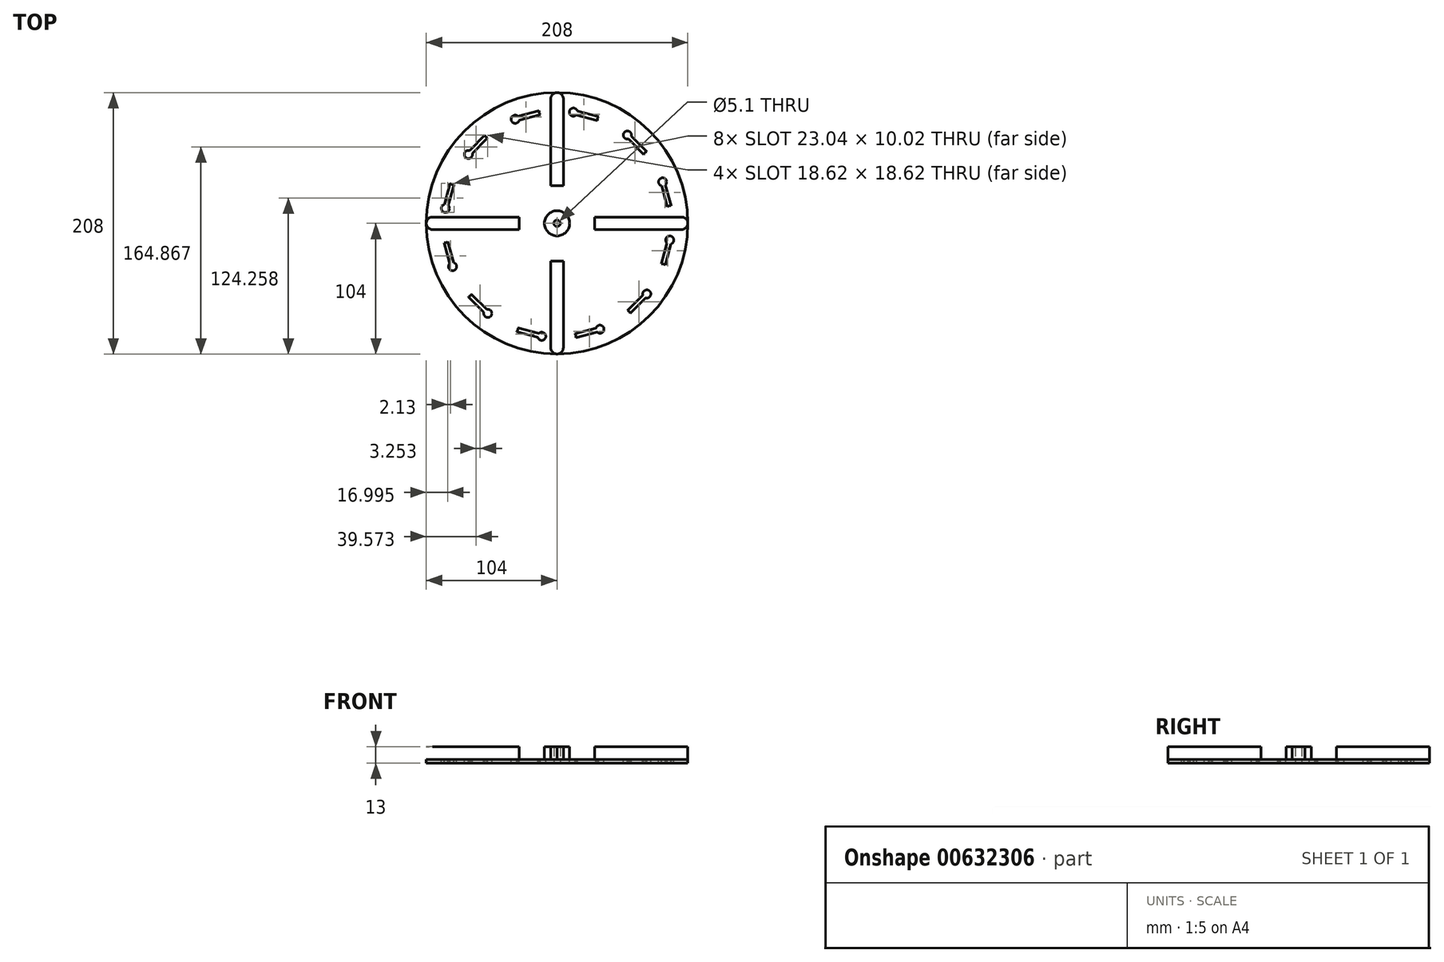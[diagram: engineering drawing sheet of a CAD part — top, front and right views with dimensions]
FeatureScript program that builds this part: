
annotation { "Feature Type Name" : "Feature", "Feature Type Description" : "" }
export const myFeature = defineFeature(function(context is Context, id is Id, definition is map)
    precondition{}
    {
        {
            var Q0;
            Q0=qCreatedBy(makeId("Top.planeOp"),FACE);
            var sketch = newSketch(context, id + "F0", { "sketchPlane" : qUnion([Q0])});
            skCircle(sketch, "E0", {"center": v(0, 0) * mm, "radius": 104 * mm});
            skSolve(sketch);
        }
        {
            var Q0;
            Q0 = qSketchRegion(id + "F0", true);
            extrude(context, id + "F1", {"entities" : qUnion([Q0]), "depth" : 3 * mm, "offsetDistance" : 25 * mm});
        }
        {
            var Q0;
            Q0=makeQuery(id+"F1.opExtrude","CAP_FACE",FACE,{"disambiguationData":[OSD([sQuery(id+"F0.wireOp",EDGE,"E0")])],"isStart":false});
            var sketch = newSketch(context, id + "F2", { "sketchPlane" : qUnion([Q0])});
            skLineSegment(sketch, "E1.bottom", {"start": v(-30, -5) * mm, "end": v(-99, -5) * mm});
            skLineSegment(sketch, "E1.top", {"start": v(-30, 5) * mm, "end": v(-99, 5) * mm});
            skLineSegment(sketch, "E1.left", {"start": v(-30, -5) * mm, "end": v(-30, 5) * mm});
            skLineSegment(sketch, "E1.right", {"start": v(-99, -5) * mm, "end": v(-99, 5) * mm});
            skPoint(sketch, "E1.middle", {"position": v(-64.5, 0) * mm});
            skArc(sketch, "E2", {"start": v(-99, -5) * mm, "mid": v(-104, 0) * mm, "end": v(-99, 5) * mm});
            skLineSegment(sketch, "E3.1.0", {"start": v(-5, -30) * mm, "end": v(-5, -99) * mm});
            skLineSegment(sketch, "E3.1.1", {"start": v(5, -30) * mm, "end": v(5, -99) * mm});
            skArc(sketch, "E3.1.2", {"start": v(5, -99) * mm, "mid": v(0, -104) * mm, "end": v(-5, -99) * mm});
            skLineSegment(sketch, "E3.1.3", {"start": v(5, -30) * mm, "end": v(-5, -30) * mm});
            skLineSegment(sketch, "E3.2.0", {"start": v(30, -5) * mm, "end": v(99, -5) * mm});
            skLineSegment(sketch, "E3.2.1", {"start": v(30, 5) * mm, "end": v(99, 5) * mm});
            skArc(sketch, "E3.2.2", {"start": v(99, 5) * mm, "mid": v(104, 0) * mm, "end": v(99, -5) * mm});
            skLineSegment(sketch, "E3.2.3", {"start": v(30, 5) * mm, "end": v(30, -5) * mm});
            skLineSegment(sketch, "E3.3.0", {"start": v(5, 30) * mm, "end": v(5, 99) * mm});
            skLineSegment(sketch, "E3.3.1", {"start": v(-5, 30) * mm, "end": v(-5, 99) * mm});
            skArc(sketch, "E3.3.2", {"start": v(-5, 99) * mm, "mid": v(0, 104) * mm, "end": v(5, 99) * mm});
            skLineSegment(sketch, "E3.3.3", {"start": v(-5, 30) * mm, "end": v(5, 30) * mm});
            skPoint(sketch, "E4.center", {"position": v(0, 0) * mm});
            skCircle(sketch, "E5", {"center": v(-34.4, -83.96) * mm, "radius": 3.25 * mm});
            skLineSegment(sketch, "E6", {"start": v(-22.88, -85.39) * mm, "end": v(-31.26, -83.14) * mm});
            skLineSegment(sketch, "E7", {"start": v(-34.4, -83.96) * mm, "end": v(-23.3, -86.93) * mm, "construction": true});
            skLineSegment(sketch, "E8.MirrorCS", {"start": v(-23.7, -88.48) * mm, "end": v(-32.08, -86.23) * mm});
            skLineSegment(sketch, "E9.MirrorCS", {"start": v(-45.97, -171.57) * mm, "end": v(-17.63, -65.8) * mm, "construction": true});
            skLineSegment(sketch, "E10.MirrorCS", {"start": v(-22.88, -85.39) * mm, "end": v(-14.5, -87.63) * mm});
            skLineSegment(sketch, "E11.MirrorCS", {"start": v(-23.7, -88.48) * mm, "end": v(-15.33, -90.72) * mm});
            skCircle(sketch, "E12.MirrorC", {"center": v(-12.19, -89.9) * mm, "radius": 3.25 * mm});
            skLineSegment(sketch, "E13.1.0", {"start": v(22.57, -85.7) * mm, "end": v(14.2, -87.94) * mm});
            skLineSegment(sketch, "E13.1.1", {"start": v(23.4, -88.79) * mm, "end": v(15.03, -91.03) * mm});
            skCircle(sketch, "E13.1.2", {"center": v(11.88, -90.22) * mm, "radius": 3.25 * mm});
            skLineSegment(sketch, "E13.1.3", {"start": v(23.4, -88.79) * mm, "end": v(31.78, -86.54) * mm});
            skLineSegment(sketch, "E13.1.4", {"start": v(22.57, -85.7) * mm, "end": v(30.95, -83.45) * mm});
            skCircle(sketch, "E13.1.5", {"center": v(34.1, -84.26) * mm, "radius": 3.25 * mm});
            skLineSegment(sketch, "E13.2.0", {"start": v(62.09, -63.23) * mm, "end": v(55.96, -69.37) * mm});
            skLineSegment(sketch, "E13.2.1", {"start": v(64.35, -65.5) * mm, "end": v(58.22, -71.63) * mm});
            skCircle(sketch, "E13.2.2", {"center": v(55.09, -72.5) * mm, "radius": 3.25 * mm});
            skLineSegment(sketch, "E13.2.3", {"start": v(64.35, -65.5) * mm, "end": v(70.48, -59.37) * mm});
            skLineSegment(sketch, "E13.2.4", {"start": v(62.09, -63.23) * mm, "end": v(68.22, -57.1) * mm});
            skCircle(sketch, "E13.2.5", {"center": v(71.35, -56.23) * mm, "radius": 3.25 * mm});
            skLineSegment(sketch, "E13.3.0", {"start": v(85.08, -24.03) * mm, "end": v(82.84, -32.4) * mm});
            skLineSegment(sketch, "E13.3.1", {"start": v(88.17, -24.85) * mm, "end": v(85.93, -33.23) * mm});
            skCircle(sketch, "E13.3.2", {"center": v(83.65, -35.55) * mm, "radius": 3.25 * mm});
            skLineSegment(sketch, "E13.3.3", {"start": v(88.17, -24.85) * mm, "end": v(90.42, -16.48) * mm});
            skLineSegment(sketch, "E13.3.4", {"start": v(85.08, -24.03) * mm, "end": v(87.32, -15.65) * mm});
            skCircle(sketch, "E13.3.5", {"center": v(89.6, -13.33) * mm, "radius": 3.25 * mm});
            skLineSegment(sketch, "E13.4.0", {"start": v(85.39, 21.43) * mm, "end": v(87.63, 13.05) * mm});
            skLineSegment(sketch, "E13.4.1", {"start": v(88.48, 22.25) * mm, "end": v(90.72, 13.88) * mm});
            skCircle(sketch, "E13.4.2", {"center": v(89.9, 10.73) * mm, "radius": 3.25 * mm});
            skLineSegment(sketch, "E13.4.3", {"start": v(88.48, 22.25) * mm, "end": v(86.23, 30.63) * mm});
            skLineSegment(sketch, "E13.4.4", {"start": v(85.39, 21.43) * mm, "end": v(83.14, 29.8) * mm});
            skCircle(sketch, "E13.4.5", {"center": v(83.96, 32.95) * mm, "radius": 3.25 * mm});
            skLineSegment(sketch, "E13.5.0", {"start": v(62.93, 60.94) * mm, "end": v(69.06, 54.81) * mm});
            skLineSegment(sketch, "E13.5.1", {"start": v(65.2, 63.2) * mm, "end": v(71.32, 57.07) * mm});
            skCircle(sketch, "E13.5.2", {"center": v(72.2, 53.94) * mm, "radius": 3.25 * mm});
            skLineSegment(sketch, "E13.5.3", {"start": v(65.2, 63.2) * mm, "end": v(59.06, 69.34) * mm});
            skLineSegment(sketch, "E13.5.4", {"start": v(62.93, 60.94) * mm, "end": v(56.8, 67.07) * mm});
            skCircle(sketch, "E13.5.5", {"center": v(55.93, 70.2) * mm, "radius": 3.25 * mm});
            skLineSegment(sketch, "E13.6.0", {"start": v(23.72, 83.93) * mm, "end": v(32.1, 81.69) * mm});
            skLineSegment(sketch, "E13.6.1", {"start": v(24.55, 87.03) * mm, "end": v(32.92, 84.78) * mm});
            skCircle(sketch, "E13.6.2", {"center": v(35.24, 82.5) * mm, "radius": 3.25 * mm});
            skLineSegment(sketch, "E13.6.3", {"start": v(24.55, 87.03) * mm, "end": v(16.17, 89.27) * mm});
            skLineSegment(sketch, "E13.6.4", {"start": v(23.72, 83.93) * mm, "end": v(15.34, 86.18) * mm});
            skCircle(sketch, "E13.6.5", {"center": v(13.02, 88.46) * mm, "radius": 3.25 * mm});
            skLineSegment(sketch, "E13.7.0", {"start": v(-21.73, 84.24) * mm, "end": v(-13.36, 86.49) * mm});
            skLineSegment(sketch, "E13.7.1", {"start": v(-22.56, 87.33) * mm, "end": v(-14.19, 89.58) * mm});
            skCircle(sketch, "E13.7.2", {"center": v(-11.04, 88.76) * mm, "radius": 3.25 * mm});
            skLineSegment(sketch, "E13.7.3", {"start": v(-22.56, 87.33) * mm, "end": v(-30.94, 85.09) * mm});
            skLineSegment(sketch, "E13.7.4", {"start": v(-21.73, 84.24) * mm, "end": v(-30.1, 82) * mm});
            skCircle(sketch, "E13.7.5", {"center": v(-33.26, 82.81) * mm, "radius": 3.25 * mm});
            skLineSegment(sketch, "E13.8.0", {"start": v(-61.25, 61.78) * mm, "end": v(-55.12, 67.91) * mm});
            skLineSegment(sketch, "E13.8.1", {"start": v(-63.51, 64.04) * mm, "end": v(-57.38, 70.18) * mm});
            skCircle(sketch, "E13.8.2", {"center": v(-54.25, 71.04) * mm, "radius": 3.25 * mm});
            skLineSegment(sketch, "E13.8.3", {"start": v(-63.51, 64.04) * mm, "end": v(-69.64, 57.91) * mm});
            skLineSegment(sketch, "E13.8.4", {"start": v(-61.25, 61.78) * mm, "end": v(-67.38, 55.65) * mm});
            skCircle(sketch, "E13.8.5", {"center": v(-70.51, 54.78) * mm, "radius": 3.25 * mm});
            skLineSegment(sketch, "E13.9.0", {"start": v(-84.24, 22.57) * mm, "end": v(-82, 30.95) * mm});
            skLineSegment(sketch, "E13.9.1", {"start": v(-87.33, 23.4) * mm, "end": v(-85.09, 31.78) * mm});
            skCircle(sketch, "E13.9.2", {"center": v(-82.81, 34.1) * mm, "radius": 3.25 * mm});
            skLineSegment(sketch, "E13.9.3", {"start": v(-87.33, 23.4) * mm, "end": v(-89.58, 15.02) * mm});
            skLineSegment(sketch, "E13.9.4", {"start": v(-84.24, 22.57) * mm, "end": v(-86.49, 14.2) * mm});
            skCircle(sketch, "E13.9.5", {"center": v(-88.76, 11.88) * mm, "radius": 3.25 * mm});
            skLineSegment(sketch, "E13.10.0", {"start": v(-84.55, -22.88) * mm, "end": v(-86.8, -14.5) * mm});
            skLineSegment(sketch, "E13.10.1", {"start": v(-87.64, -23.7) * mm, "end": v(-89.88, -15.33) * mm});
            skCircle(sketch, "E13.10.2", {"center": v(-89.07, -12.19) * mm, "radius": 3.25 * mm});
            skLineSegment(sketch, "E13.10.3", {"start": v(-87.64, -23.7) * mm, "end": v(-85.4, -32.08) * mm});
            skLineSegment(sketch, "E13.10.4", {"start": v(-84.55, -22.88) * mm, "end": v(-82.3, -31.26) * mm});
            skCircle(sketch, "E13.10.5", {"center": v(-83.12, -34.4) * mm, "radius": 3.25 * mm});
            skLineSegment(sketch, "E13.11.0", {"start": v(-62.09, -62.4) * mm, "end": v(-68.22, -56.26) * mm});
            skLineSegment(sketch, "E13.11.1", {"start": v(-64.35, -64.66) * mm, "end": v(-70.48, -58.53) * mm});
            skCircle(sketch, "E13.11.2", {"center": v(-71.35, -55.4) * mm, "radius": 3.25 * mm});
            skLineSegment(sketch, "E13.11.3", {"start": v(-64.35, -64.66) * mm, "end": v(-58.22, -70.8) * mm});
            skLineSegment(sketch, "E13.11.4", {"start": v(-62.09, -62.4) * mm, "end": v(-55.96, -68.53) * mm});
            skCircle(sketch, "E13.11.5", {"center": v(-55.09, -71.66) * mm, "radius": 3.25 * mm});
            skLineSegment(sketch, "E14", {"start": v(0, 0) * mm, "end": v(-23.3, -86.93) * mm, "construction": true});
            skCircle(sketch, "E15", {"center": v(0, 0) * mm, "radius": 10 * mm});
            skCircle(sketch, "E16", {"center": v(0, 0) * mm, "radius": 2.55 * mm});
            skSolve(sketch);
        }
        {
            var Q0;
            Q0=makeQuery(id+"F2.imprint","IMPRINT",FACE,{"disambiguationData":[TD([[makeQuery(id+"F2.imprint","IMPRINT",EDGE,{"derivedFrom":sQuery(id+"F2.wireOp",EDGE,"E1.bottom")}),-1.0]])]});
            var Q1;
            {var subQ0=sQuery(id+"F2.wireOp",EDGE,"E1.right");Q1=makeQuery(id+"F2.imprint","IMPRINT",FACE,{"disambiguationData":[TD([[makeQuery(id+"F2.imprint","IMPRINT",EDGE,{"derivedFrom":subQ0}),1.0]])]});}
            var Q2;
            Q2=makeQuery(id+"F2.imprint","IMPRINT",FACE,{"disambiguationData":[TD([[makeQuery(id+"F2.imprint","IMPRINT",EDGE,{"derivedFrom":sQuery(id+"F2.wireOp",EDGE,"1YY4uECu-RtR1-OI2Z-D8cp-1v98Y9N5imrY")}),1.0]])]});
            var Q3;
            {var subQ1=sQuery(id+"F2.wireOp",EDGE,"E3.3.0");Q3=makeQuery(id+"F2.imprint","IMPRINT",FACE,{"disambiguationData":[TD([[makeQuery(id+"F2.imprint","IMPRINT",EDGE,{"derivedFrom":subQ1}),1.0]])]});}
            var Q4;
            {var subQ1=sQuery(id+"F2.wireOp",EDGE,"E3.1.0");Q4=makeQuery(id+"F2.imprint","IMPRINT",FACE,{"disambiguationData":[TD([[makeQuery(id+"F2.imprint","IMPRINT",EDGE,{"derivedFrom":subQ1}),1.0]])]});}
            var Q5;
            {var subQ1=sQuery(id+"F2.wireOp",EDGE,"E3.2.0");Q5=makeQuery(id+"F2.imprint","IMPRINT",FACE,{"disambiguationData":[TD([[makeQuery(id+"F2.imprint","IMPRINT",EDGE,{"derivedFrom":subQ1}),1.0]])]});}
            var Q6;
            Q6=makeQuery(id+"F2.imprint","IMPRINT",FACE,{"disambiguationData":[TD([[makeQuery(id+"F2.imprint","IMPRINT",EDGE,{"derivedFrom":sQuery(id+"F2.wireOp",EDGE,"E15")}),1.0]])]});
            extrude(context, id + "F3", {"entities" : qUnion([Q0, Q1, Q2, Q3, Q4, Q5, Q6]), "operationType" : NewBodyOperationType.ADD, "depth" : 10 * mm, "offsetDistance" : 25 * mm});
        }
        {
            var Q0;
            {var subQ0=sQuery(id+"F2.wireOp",EDGE,"E13.9.5");var subQ1=makeQuery(id+"F2.imprint","INTERSECT",VERTEX,{"derivedFrom":[sQuery(id+"F2.wireOp",EDGE,"E13.9.3"),subQ0]});Q0=makeQuery(id+"F2.imprint","IMPRINT",FACE,{"disambiguationData":[TD([[makeQuery(id+"F2.imprint","IMPRINT",EDGE,{"disambiguationData":[TD([[subQ1,-1.0]])],"derivedFrom":subQ0}),1.0]])]});}
            var Q1;
            {var subQ2=sQuery(id+"F2.wireOp",EDGE,"E13.9.0");Q1=makeQuery(id+"F2.imprint","IMPRINT",FACE,{"disambiguationData":[TD([[makeQuery(id+"F2.imprint","IMPRINT",EDGE,{"derivedFrom":subQ2}),1.0]])]});}
            var Q2;
            {var subQ0=sQuery(id+"F2.wireOp",EDGE,"E13.9.2");var subQ1=makeQuery(id+"F2.imprint","INTERSECT",VERTEX,{"derivedFrom":[sQuery(id+"F2.wireOp",EDGE,"E13.9.0"),subQ0]});Q2=makeQuery(id+"F2.imprint","IMPRINT",FACE,{"disambiguationData":[TD([[makeQuery(id+"F2.imprint","IMPRINT",EDGE,{"disambiguationData":[TD([[subQ1,1.0]])],"derivedFrom":subQ0}),-1.0]])]});}
            var Q3;
            {var subQ0=sQuery(id+"F2.wireOp",EDGE,"E13.8.5");var subQ1=makeQuery(id+"F2.imprint","INTERSECT",VERTEX,{"derivedFrom":[sQuery(id+"F2.wireOp",EDGE,"E13.8.3"),subQ0]});Q3=makeQuery(id+"F2.imprint","IMPRINT",FACE,{"disambiguationData":[TD([[makeQuery(id+"F2.imprint","IMPRINT",EDGE,{"disambiguationData":[TD([[subQ1,-1.0]])],"derivedFrom":subQ0}),1.0]])]});}
            var Q4;
            {var subQ2=sQuery(id+"F2.wireOp",EDGE,"E13.8.0");Q4=makeQuery(id+"F2.imprint","IMPRINT",FACE,{"disambiguationData":[TD([[makeQuery(id+"F2.imprint","IMPRINT",EDGE,{"derivedFrom":subQ2}),1.0]])]});}
            var Q5;
            {var subQ0=sQuery(id+"F2.wireOp",EDGE,"E13.8.2");var subQ1=makeQuery(id+"F2.imprint","INTERSECT",VERTEX,{"derivedFrom":[sQuery(id+"F2.wireOp",EDGE,"E13.8.0"),subQ0]});Q5=makeQuery(id+"F2.imprint","IMPRINT",FACE,{"disambiguationData":[TD([[makeQuery(id+"F2.imprint","IMPRINT",EDGE,{"disambiguationData":[TD([[subQ1,1.0]])],"derivedFrom":subQ0}),-1.0]])]});}
            var Q6;
            {var subQ0=sQuery(id+"F2.wireOp",EDGE,"E13.7.5");var subQ1=makeQuery(id+"F2.imprint","INTERSECT",VERTEX,{"derivedFrom":[sQuery(id+"F2.wireOp",EDGE,"E13.7.3"),subQ0]});Q6=makeQuery(id+"F2.imprint","IMPRINT",FACE,{"disambiguationData":[TD([[makeQuery(id+"F2.imprint","IMPRINT",EDGE,{"disambiguationData":[TD([[subQ1,-1.0]])],"derivedFrom":subQ0}),1.0]])]});}
            var Q7;
            {var subQ2=sQuery(id+"F2.wireOp",EDGE,"E13.7.0");Q7=makeQuery(id+"F2.imprint","IMPRINT",FACE,{"disambiguationData":[TD([[makeQuery(id+"F2.imprint","IMPRINT",EDGE,{"derivedFrom":subQ2}),1.0]])]});}
            var Q8;
            {var subQ0=sQuery(id+"F2.wireOp",EDGE,"E13.7.2");var subQ1=makeQuery(id+"F2.imprint","INTERSECT",VERTEX,{"derivedFrom":[sQuery(id+"F2.wireOp",EDGE,"E13.7.0"),subQ0]});Q8=makeQuery(id+"F2.imprint","IMPRINT",FACE,{"disambiguationData":[TD([[makeQuery(id+"F2.imprint","IMPRINT",EDGE,{"disambiguationData":[TD([[subQ1,1.0]])],"derivedFrom":subQ0}),-1.0]])]});}
            var Q9;
            {var subQ0=sQuery(id+"F2.wireOp",EDGE,"E13.6.5");var subQ1=makeQuery(id+"F2.imprint","INTERSECT",VERTEX,{"derivedFrom":[sQuery(id+"F2.wireOp",EDGE,"E13.6.3"),subQ0]});Q9=makeQuery(id+"F2.imprint","IMPRINT",FACE,{"disambiguationData":[TD([[makeQuery(id+"F2.imprint","IMPRINT",EDGE,{"disambiguationData":[TD([[subQ1,-1.0]])],"derivedFrom":subQ0}),1.0]])]});}
            var Q10;
            {var subQ2=sQuery(id+"F2.wireOp",EDGE,"E13.6.0");Q10=makeQuery(id+"F2.imprint","IMPRINT",FACE,{"disambiguationData":[TD([[makeQuery(id+"F2.imprint","IMPRINT",EDGE,{"derivedFrom":subQ2}),1.0]])]});}
            var Q11;
            {var subQ0=sQuery(id+"F2.wireOp",EDGE,"E13.6.2");var subQ1=makeQuery(id+"F2.imprint","INTERSECT",VERTEX,{"derivedFrom":[sQuery(id+"F2.wireOp",EDGE,"E13.6.0"),subQ0]});Q11=makeQuery(id+"F2.imprint","IMPRINT",FACE,{"disambiguationData":[TD([[makeQuery(id+"F2.imprint","IMPRINT",EDGE,{"disambiguationData":[TD([[subQ1,1.0]])],"derivedFrom":subQ0}),-1.0]])]});}
            var Q12;
            {var subQ0=sQuery(id+"F2.wireOp",EDGE,"E13.5.5");var subQ1=makeQuery(id+"F2.imprint","INTERSECT",VERTEX,{"derivedFrom":[sQuery(id+"F2.wireOp",EDGE,"E13.5.3"),subQ0]});Q12=makeQuery(id+"F2.imprint","IMPRINT",FACE,{"disambiguationData":[TD([[makeQuery(id+"F2.imprint","IMPRINT",EDGE,{"disambiguationData":[TD([[subQ1,-1.0]])],"derivedFrom":subQ0}),1.0]])]});}
            var Q13;
            {var subQ2=sQuery(id+"F2.wireOp",EDGE,"E13.5.0");Q13=makeQuery(id+"F2.imprint","IMPRINT",FACE,{"disambiguationData":[TD([[makeQuery(id+"F2.imprint","IMPRINT",EDGE,{"derivedFrom":subQ2}),1.0]])]});}
            var Q14;
            {var subQ0=sQuery(id+"F2.wireOp",EDGE,"E13.5.2");var subQ1=makeQuery(id+"F2.imprint","INTERSECT",VERTEX,{"derivedFrom":[sQuery(id+"F2.wireOp",EDGE,"E13.5.0"),subQ0]});Q14=makeQuery(id+"F2.imprint","IMPRINT",FACE,{"disambiguationData":[TD([[makeQuery(id+"F2.imprint","IMPRINT",EDGE,{"disambiguationData":[TD([[subQ1,1.0]])],"derivedFrom":subQ0}),-1.0]])]});}
            var Q15;
            {var subQ0=sQuery(id+"F2.wireOp",EDGE,"E13.4.5");var subQ1=makeQuery(id+"F2.imprint","INTERSECT",VERTEX,{"derivedFrom":[sQuery(id+"F2.wireOp",EDGE,"E13.4.3"),subQ0]});Q15=makeQuery(id+"F2.imprint","IMPRINT",FACE,{"disambiguationData":[TD([[makeQuery(id+"F2.imprint","IMPRINT",EDGE,{"disambiguationData":[TD([[subQ1,-1.0]])],"derivedFrom":subQ0}),1.0]])]});}
            var Q16;
            {var subQ2=sQuery(id+"F2.wireOp",EDGE,"E13.4.0");Q16=makeQuery(id+"F2.imprint","IMPRINT",FACE,{"disambiguationData":[TD([[makeQuery(id+"F2.imprint","IMPRINT",EDGE,{"derivedFrom":subQ2}),1.0]])]});}
            var Q17;
            {var subQ0=sQuery(id+"F2.wireOp",EDGE,"E13.4.2");var subQ1=makeQuery(id+"F2.imprint","INTERSECT",VERTEX,{"derivedFrom":[sQuery(id+"F2.wireOp",EDGE,"E13.4.0"),subQ0]});Q17=makeQuery(id+"F2.imprint","IMPRINT",FACE,{"disambiguationData":[TD([[makeQuery(id+"F2.imprint","IMPRINT",EDGE,{"disambiguationData":[TD([[subQ1,1.0]])],"derivedFrom":subQ0}),-1.0]])]});}
            var Q18;
            {var subQ0=sQuery(id+"F2.wireOp",EDGE,"E13.3.5");var subQ1=makeQuery(id+"F2.imprint","INTERSECT",VERTEX,{"derivedFrom":[sQuery(id+"F2.wireOp",EDGE,"E13.3.3"),subQ0]});Q18=makeQuery(id+"F2.imprint","IMPRINT",FACE,{"disambiguationData":[TD([[makeQuery(id+"F2.imprint","IMPRINT",EDGE,{"disambiguationData":[TD([[subQ1,-1.0]])],"derivedFrom":subQ0}),1.0]])]});}
            var Q19;
            {var subQ2=sQuery(id+"F2.wireOp",EDGE,"E13.3.0");Q19=makeQuery(id+"F2.imprint","IMPRINT",FACE,{"disambiguationData":[TD([[makeQuery(id+"F2.imprint","IMPRINT",EDGE,{"derivedFrom":subQ2}),1.0]])]});}
            var Q20;
            {var subQ0=sQuery(id+"F2.wireOp",EDGE,"E13.3.2");var subQ1=makeQuery(id+"F2.imprint","INTERSECT",VERTEX,{"derivedFrom":[sQuery(id+"F2.wireOp",EDGE,"E13.3.0"),subQ0]});Q20=makeQuery(id+"F2.imprint","IMPRINT",FACE,{"disambiguationData":[TD([[makeQuery(id+"F2.imprint","IMPRINT",EDGE,{"disambiguationData":[TD([[subQ1,1.0]])],"derivedFrom":subQ0}),-1.0]])]});}
            var Q21;
            {var subQ0=sQuery(id+"F2.wireOp",EDGE,"E13.2.5");var subQ1=makeQuery(id+"F2.imprint","INTERSECT",VERTEX,{"derivedFrom":[sQuery(id+"F2.wireOp",EDGE,"E13.2.3"),subQ0]});Q21=makeQuery(id+"F2.imprint","IMPRINT",FACE,{"disambiguationData":[TD([[makeQuery(id+"F2.imprint","IMPRINT",EDGE,{"disambiguationData":[TD([[subQ1,-1.0]])],"derivedFrom":subQ0}),1.0]])]});}
            var Q22;
            {var subQ2=sQuery(id+"F2.wireOp",EDGE,"E13.2.0");Q22=makeQuery(id+"F2.imprint","IMPRINT",FACE,{"disambiguationData":[TD([[makeQuery(id+"F2.imprint","IMPRINT",EDGE,{"derivedFrom":subQ2}),1.0]])]});}
            var Q23;
            {var subQ0=sQuery(id+"F2.wireOp",EDGE,"E13.2.2");var subQ1=makeQuery(id+"F2.imprint","INTERSECT",VERTEX,{"derivedFrom":[sQuery(id+"F2.wireOp",EDGE,"E13.2.0"),subQ0]});Q23=makeQuery(id+"F2.imprint","IMPRINT",FACE,{"disambiguationData":[TD([[makeQuery(id+"F2.imprint","IMPRINT",EDGE,{"disambiguationData":[TD([[subQ1,1.0]])],"derivedFrom":subQ0}),-1.0]])]});}
            var Q24;
            {var subQ0=sQuery(id+"F2.wireOp",EDGE,"E13.1.5");var subQ1=makeQuery(id+"F2.imprint","INTERSECT",VERTEX,{"derivedFrom":[sQuery(id+"F2.wireOp",EDGE,"E13.1.3"),subQ0]});Q24=makeQuery(id+"F2.imprint","IMPRINT",FACE,{"disambiguationData":[TD([[makeQuery(id+"F2.imprint","IMPRINT",EDGE,{"disambiguationData":[TD([[subQ1,-1.0]])],"derivedFrom":subQ0}),1.0]])]});}
            var Q25;
            {var subQ2=sQuery(id+"F2.wireOp",EDGE,"E13.1.0");Q25=makeQuery(id+"F2.imprint","IMPRINT",FACE,{"disambiguationData":[TD([[makeQuery(id+"F2.imprint","IMPRINT",EDGE,{"derivedFrom":subQ2}),1.0]])]});}
            var Q26;
            {var subQ0=sQuery(id+"F2.wireOp",EDGE,"E13.1.2");var subQ1=makeQuery(id+"F2.imprint","INTERSECT",VERTEX,{"derivedFrom":[sQuery(id+"F2.wireOp",EDGE,"E13.1.0"),subQ0]});Q26=makeQuery(id+"F2.imprint","IMPRINT",FACE,{"disambiguationData":[TD([[makeQuery(id+"F2.imprint","IMPRINT",EDGE,{"disambiguationData":[TD([[subQ1,1.0]])],"derivedFrom":subQ0}),-1.0]])]});}
            var Q27;
            {var subQ0=sQuery(id+"F2.wireOp",EDGE,"E12.MirrorC");var subQ1=makeQuery(id+"F2.imprint","INTERSECT",VERTEX,{"derivedFrom":[sQuery(id+"F2.wireOp",EDGE,"E10.MirrorCS"),subQ0]});Q27=makeQuery(id+"F2.imprint","IMPRINT",FACE,{"disambiguationData":[TD([[makeQuery(id+"F2.imprint","IMPRINT",EDGE,{"disambiguationData":[TD([[subQ1,1.0]])],"derivedFrom":subQ0}),1.0]])]});}
            var Q28;
            {var subQ2=sQuery(id+"F2.wireOp",EDGE,"E6");Q28=makeQuery(id+"F2.imprint","IMPRINT",FACE,{"disambiguationData":[TD([[makeQuery(id+"F2.imprint","IMPRINT",EDGE,{"derivedFrom":subQ2}),1.0]])]});}
            var Q29;
            {var subQ0=sQuery(id+"F2.wireOp",EDGE,"E5");var subQ1=makeQuery(id+"F2.imprint","INTERSECT",VERTEX,{"derivedFrom":[sQuery(id+"F2.wireOp",EDGE,"E6"),subQ0]});Q29=makeQuery(id+"F2.imprint","IMPRINT",FACE,{"disambiguationData":[TD([[makeQuery(id+"F2.imprint","IMPRINT",EDGE,{"disambiguationData":[TD([[subQ1,1.0]])],"derivedFrom":subQ0}),-1.0]])]});}
            var Q30;
            {var subQ0=sQuery(id+"F2.wireOp",EDGE,"E13.11.5");var subQ1=makeQuery(id+"F2.imprint","INTERSECT",VERTEX,{"derivedFrom":[sQuery(id+"F2.wireOp",EDGE,"E13.11.3"),subQ0]});Q30=makeQuery(id+"F2.imprint","IMPRINT",FACE,{"disambiguationData":[TD([[makeQuery(id+"F2.imprint","IMPRINT",EDGE,{"disambiguationData":[TD([[subQ1,-1.0]])],"derivedFrom":subQ0}),1.0]])]});}
            var Q31;
            {var subQ2=sQuery(id+"F2.wireOp",EDGE,"E13.11.0");Q31=makeQuery(id+"F2.imprint","IMPRINT",FACE,{"disambiguationData":[TD([[makeQuery(id+"F2.imprint","IMPRINT",EDGE,{"derivedFrom":subQ2}),1.0]])]});}
            var Q32;
            {var subQ0=sQuery(id+"F2.wireOp",EDGE,"E13.11.2");var subQ1=makeQuery(id+"F2.imprint","INTERSECT",VERTEX,{"derivedFrom":[sQuery(id+"F2.wireOp",EDGE,"E13.11.0"),subQ0]});Q32=makeQuery(id+"F2.imprint","IMPRINT",FACE,{"disambiguationData":[TD([[makeQuery(id+"F2.imprint","IMPRINT",EDGE,{"disambiguationData":[TD([[subQ1,1.0]])],"derivedFrom":subQ0}),-1.0]])]});}
            var Q33;
            {var subQ0=sQuery(id+"F2.wireOp",EDGE,"E13.10.5");var subQ1=makeQuery(id+"F2.imprint","INTERSECT",VERTEX,{"derivedFrom":[sQuery(id+"F2.wireOp",EDGE,"E13.10.3"),subQ0]});Q33=makeQuery(id+"F2.imprint","IMPRINT",FACE,{"disambiguationData":[TD([[makeQuery(id+"F2.imprint","IMPRINT",EDGE,{"disambiguationData":[TD([[subQ1,-1.0]])],"derivedFrom":subQ0}),1.0]])]});}
            var Q34;
            {var subQ2=sQuery(id+"F2.wireOp",EDGE,"E13.10.0");Q34=makeQuery(id+"F2.imprint","IMPRINT",FACE,{"disambiguationData":[TD([[makeQuery(id+"F2.imprint","IMPRINT",EDGE,{"derivedFrom":subQ2}),1.0]])]});}
            var Q35;
            {var subQ0=sQuery(id+"F2.wireOp",EDGE,"E13.10.2");var subQ1=makeQuery(id+"F2.imprint","INTERSECT",VERTEX,{"derivedFrom":[sQuery(id+"F2.wireOp",EDGE,"E13.10.0"),subQ0]});Q35=makeQuery(id+"F2.imprint","IMPRINT",FACE,{"disambiguationData":[TD([[makeQuery(id+"F2.imprint","IMPRINT",EDGE,{"disambiguationData":[TD([[subQ1,1.0]])],"derivedFrom":subQ0}),-1.0]])]});}
            var Q36;
            Q36=makeQuery(id+"F2.imprint","IMPRINT",FACE,{"disambiguationData":[TD([[makeQuery(id+"F2.imprint","IMPRINT",EDGE,{"derivedFrom":sQuery(id+"F2.wireOp",EDGE,"9r0xNKpm-683T-9OrH-TS5f-xUMtmP6rM6P2")}),1.0]])]});
            var Q37;
            Q37=makeQuery(id+"F2.imprint","IMPRINT",FACE,{"disambiguationData":[TD([[makeQuery(id+"F2.imprint","IMPRINT",EDGE,{"derivedFrom":sQuery(id+"F2.wireOp",EDGE,"E16")}),1.0]])]});
            var Q38;
            Q38=makeQuery(id+"F1.opExtrude","CAP_FACE",FACE,{"disambiguationData":[OSD([sQuery(id+"F0.wireOp",EDGE,"E0")])],"isStart":true});
            extrude(context, id + "F4", {"entities" : qUnion([Q0, Q1, Q2, Q3, Q4, Q5, Q6, Q7, Q8, Q9, Q10, Q11, Q12, Q13, Q14, Q15, Q16, Q17, Q18, Q19, Q20, Q21, Q22, Q23, Q24, Q25, Q26, Q27, Q28, Q29, Q30, Q31, Q32, Q33, Q34, Q35, Q36, Q37]), "operationType" : NewBodyOperationType.REMOVE, "endBound" : BoundingType.UP_TO_SURFACE, "oppositeDirection" : true, "depth" : 25 * mm, "endBoundEntityFace" : qUnion([Q38]), "offsetDistance" : 25 * mm});
        }
    });
